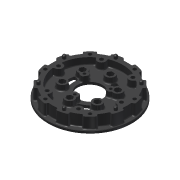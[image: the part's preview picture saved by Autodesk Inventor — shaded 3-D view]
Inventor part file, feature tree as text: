
AUTODESK INVENTOR PART (.ipt)
format: ipt  version: 2013 (Build 170138000, 138)  size: 1,574,400 bytes
history: native  units: in
note: dims shown in document units (in); Inventor stores cm internally (conversion verified against a paired STEP export)
features: fillet x1, other x1, imported_body x1
ambient origin geometry x8: Origin, YZ Plane, XZ Plane, XY Plane, X Axis, Y Axis, Z Axis, Center Point
feature tree (3):
  fillet  "Fillet18"  [1 undecoded]
  other  "217-2588-001 Rev41"
  imported_body  "Base1"
note: 1 required parameter value undecoded (feature->parameter linkage not recoverable at this tier; creation-order binding heuristic only, values carry confidence <= 0.55)
